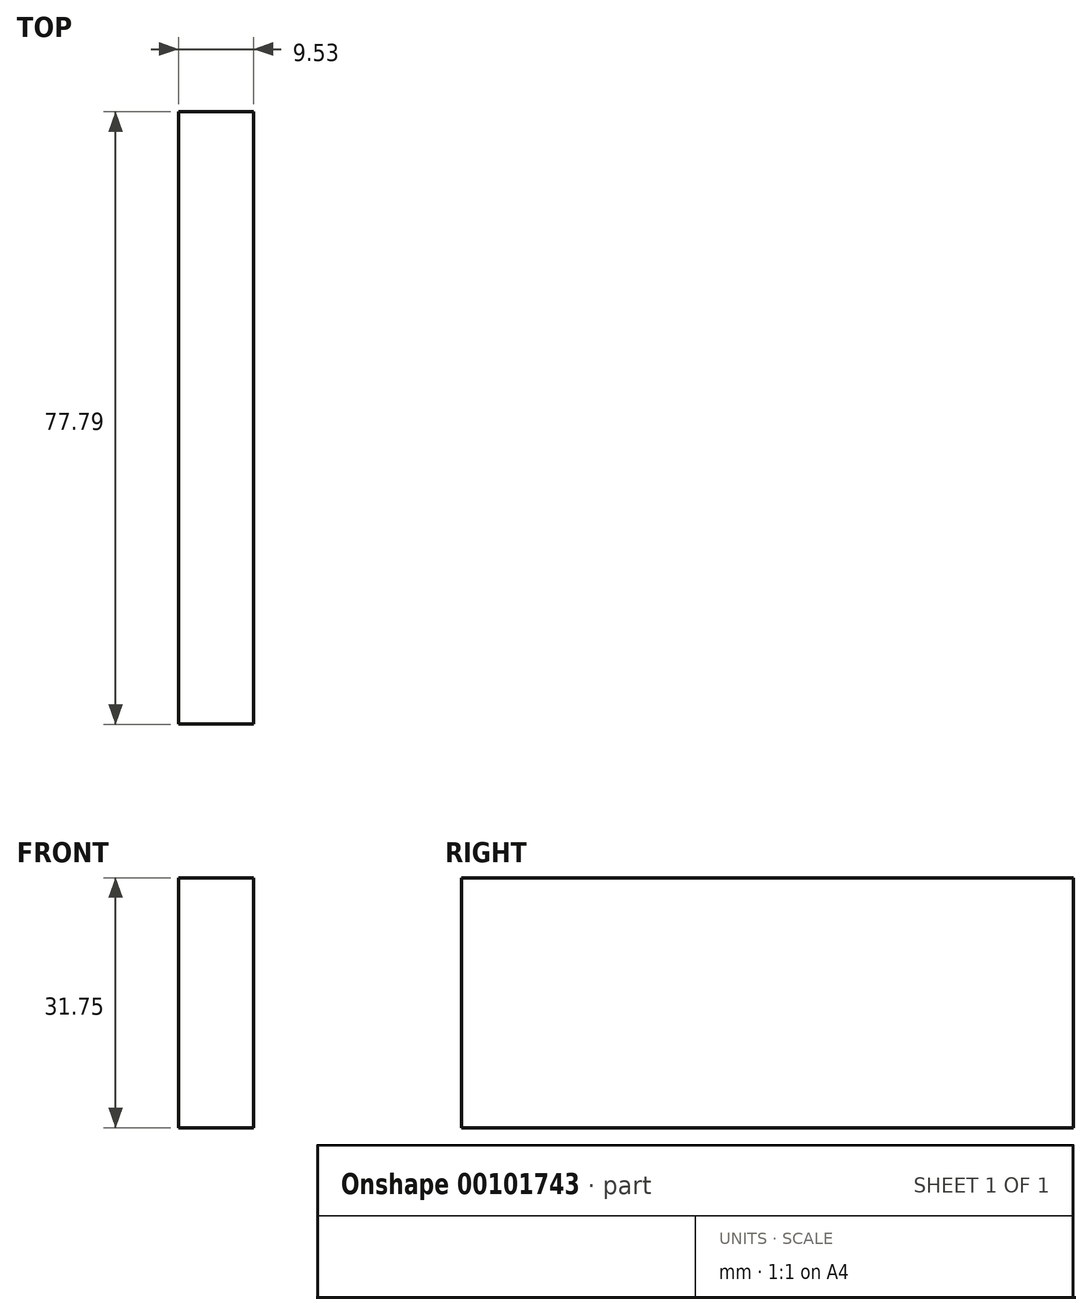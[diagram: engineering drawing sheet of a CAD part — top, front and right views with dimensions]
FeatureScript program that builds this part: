
annotation { "Feature Type Name" : "Feature", "Feature Type Description" : "" }
export const myFeature = defineFeature(function(context is Context, id is Id, definition is map)
    precondition{}
    {
        {
            var Q0;
            Q0=qCreatedBy(makeId("Right.planeOp"),FACE);
            var sketch = newSketch(context, id + "F0", { "sketchPlane" : qUnion([Q0])});
            skLineSegment(sketch, "E0.bottom", {"start": v(-39.18, 47.82) * mm, "end": v(38.61, 47.82) * mm});
            skLineSegment(sketch, "E0.top", {"start": v(-39.18, 16.07) * mm, "end": v(38.61, 16.07) * mm});
            skLineSegment(sketch, "E0.left", {"start": v(-39.18, 47.82) * mm, "end": v(-39.18, 16.07) * mm});
            skLineSegment(sketch, "E0.right", {"start": v(38.61, 47.82) * mm, "end": v(38.61, 16.07) * mm});
            skSolve(sketch);
        }
        {
            var Q0;
            Q0 = qSketchRegion(id + "F0", true);
            extrude(context, id + "F1", {"entities" : qUnion([Q0]), "depth" : 9.52 * mm});
        }
    });
